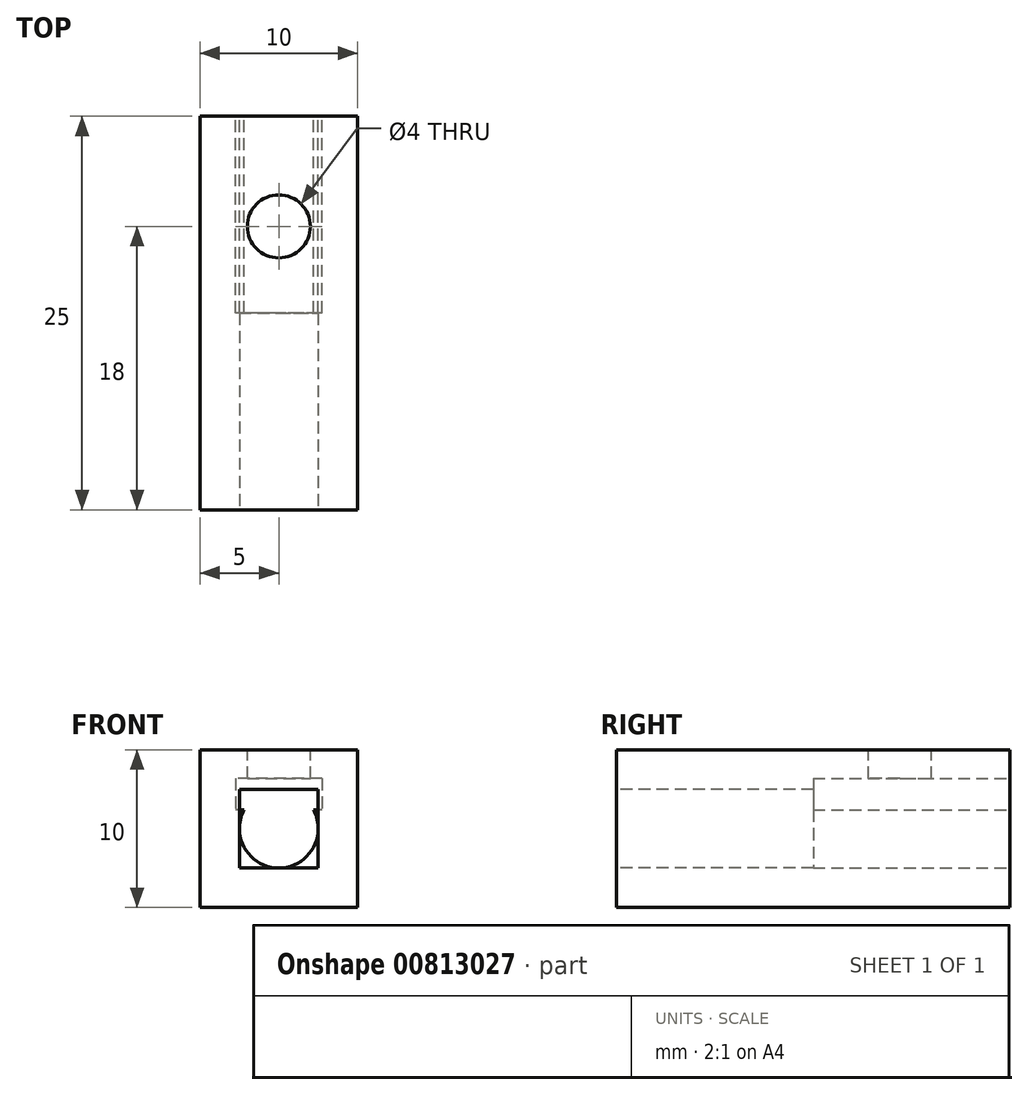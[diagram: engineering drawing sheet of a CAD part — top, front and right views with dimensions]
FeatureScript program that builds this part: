
annotation { "Feature Type Name" : "Feature", "Feature Type Description" : "" }
export const myFeature = defineFeature(function(context is Context, id is Id, definition is map)
    precondition{}
    {
        {
            var Q0;
            Q0=qCreatedBy(makeId("Front.planeOp"),FACE);
            var sketch = newSketch(context, id + "F0", { "sketchPlane" : qUnion([Q0])});
            skLineSegment(sketch, "E0.bottom", {"start": v(-5, 5) * mm, "end": v(5, 5) * mm});
            skLineSegment(sketch, "E0.top", {"start": v(-5, -5) * mm, "end": v(5, -5) * mm});
            skLineSegment(sketch, "E0.left", {"start": v(-5, 5) * mm, "end": v(-5, -5) * mm});
            skLineSegment(sketch, "E0.right", {"start": v(5, 5) * mm, "end": v(5, -5) * mm});
            skSolve(sketch);
        }
        {
            var Q0;
            Q0=makeQuery(id+"F0.imprint","IMPRINT",FACE,{"disambiguationData":[TD([[makeQuery(id+"F0.imprint","IMPRINT",EDGE,{"derivedFrom":sQuery(id+"F0.wireOp",EDGE,"E0.bottom")}),-1.0]])]});
            extrude(context, id + "F1", {"entities" : qUnion([Q0]), "depth" : 25 * mm, "offsetDistance" : 25 * mm});
        }
        {
            var Q0;
            Q0=makeQuery(id+"F1.opExtrude","CAP_FACE",FACE,{"disambiguationData":[OSD([sQuery(id+"F0.wireOp",EDGE,"E0.bottom"),sQuery(id+"F0.wireOp",EDGE,"E0.top"),sQuery(id+"F0.wireOp",EDGE,"E0.left"),sQuery(id+"F0.wireOp",EDGE,"E0.right")])],"isStart":false});
            var sketch = newSketch(context, id + "F2", { "sketchPlane" : qUnion([Q0])});
            skLineSegment(sketch, "E1.bottom", {"start": v(-2.5, 2.5) * mm, "end": v(2.5, 2.5) * mm});
            skLineSegment(sketch, "E1.top", {"start": v(-2.5, -2.5) * mm, "end": v(2.5, -2.5) * mm});
            skLineSegment(sketch, "E1.left", {"start": v(-2.5, 2.5) * mm, "end": v(-2.5, -2.5) * mm});
            skLineSegment(sketch, "E1.right", {"start": v(2.5, 2.5) * mm, "end": v(2.5, -2.5) * mm});
            skSolve(sketch);
        }
        {
            var Q0;
            Q0=makeQuery(id+"F2.imprint","IMPRINT",FACE,{"disambiguationData":[TD([[makeQuery(id+"F2.imprint","IMPRINT",EDGE,{"derivedFrom":sQuery(id+"F2.wireOp",EDGE,"E1.bottom")}),-1.0]])]});
            extrude(context, id + "F3", {"entities" : qUnion([Q0]), "operationType" : NewBodyOperationType.REMOVE, "oppositeDirection" : true, "depth" : 12.5 * mm, "offsetDistance" : 25 * mm});
        }
        {
            var Q0;
            Q0=makeQuery(id+"F1.opExtrude","CAP_FACE",FACE,{"disambiguationData":[OSD([sQuery(id+"F0.wireOp",EDGE,"E0.bottom"),sQuery(id+"F0.wireOp",EDGE,"E0.top"),sQuery(id+"F0.wireOp",EDGE,"E0.left"),sQuery(id+"F0.wireOp",EDGE,"E0.right")])],"isStart":true});
            var sketch = newSketch(context, id + "F4", { "sketchPlane" : qUnion([Q0])});
            skCircle(sketch, "E2", {"center": v(0, 0) * mm, "radius": 2.5 * mm});
            skLineSegment(sketch, "E3.bottom", {"start": v(-2.75, 3.18) * mm, "end": v(2.75, 3.18) * mm});
            skLineSegment(sketch, "E3.top", {"start": v(-2.75, 1.18) * mm, "end": v(2.75, 1.18) * mm});
            skLineSegment(sketch, "E3.left", {"start": v(-2.75, 3.18) * mm, "end": v(-2.75, 1.18) * mm});
            skLineSegment(sketch, "E3.right", {"start": v(2.75, 3.18) * mm, "end": v(2.75, 1.18) * mm});
            skSolve(sketch);
        }
        {
            var Q0;
            Q0=makeQuery(id+"F4.imprint","IMPRINT",FACE,{"disambiguationData":[TD([[makeQuery(id+"F4.imprint","IMPRINT",EDGE,{"derivedFrom":sQuery(id+"F4.wireOp",EDGE,"E2")}),1.0]])]});
            var Q1;
            Q1=makeQuery(id+"F4.imprint","IMPRINT",FACE,{"disambiguationData":[TD([[makeQuery(id+"F4.imprint","IMPRINT",EDGE,{"derivedFrom":sQuery(id+"F4.wireOp",EDGE,"E3.bottom")}),-1.0]])]});
            extrude(context, id + "F5", {"entities" : qUnion([Q0, Q1]), "operationType" : NewBodyOperationType.REMOVE, "oppositeDirection" : true, "depth" : 12.5 * mm, "offsetDistance" : 25 * mm});
        }
        {
            var Q0;
            Q0=makeQuery(id+"F1.opExtrude","SWEPT_FACE",FACE,{"disambiguationData":[OSD([sQuery(id+"F0.wireOp",EDGE,"E0.bottom")])]});
            var sketch = newSketch(context, id + "F6", { "sketchPlane" : qUnion([Q0])});
            skCircle(sketch, "E4", {"center": v(0, -7) * mm, "radius": 2 * mm});
            skSolve(sketch);
        }
        {
            var Q0;
            Q0=makeQuery(id+"F6.imprint","IMPRINT",FACE,{"disambiguationData":[TD([[makeQuery(id+"F6.imprint","IMPRINT",EDGE,{"derivedFrom":sQuery(id+"F6.wireOp",EDGE,"E4")}),1.0]])]});
            extrude(context, id + "F7", {"entities" : qUnion([Q0]), "operationType" : NewBodyOperationType.REMOVE, "oppositeDirection" : true, "depth" : 5 * mm, "offsetDistance" : 25 * mm});
        }
    });
